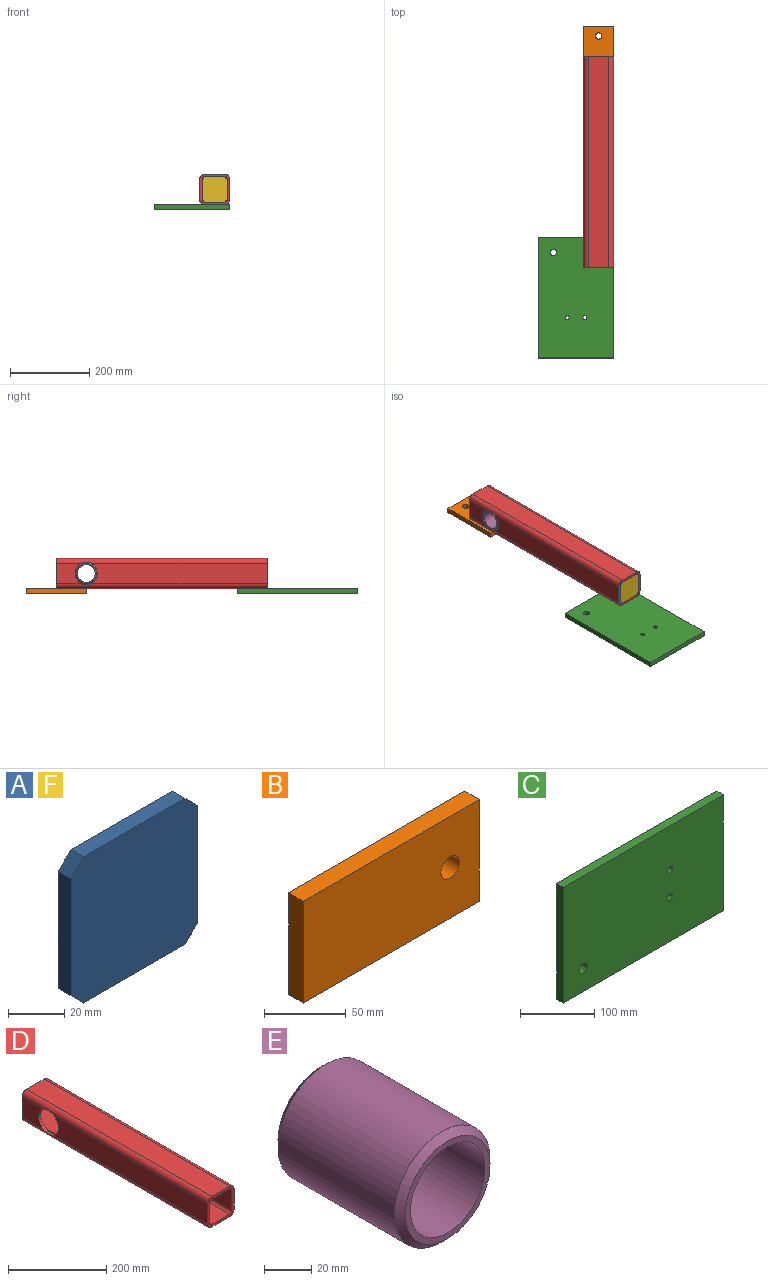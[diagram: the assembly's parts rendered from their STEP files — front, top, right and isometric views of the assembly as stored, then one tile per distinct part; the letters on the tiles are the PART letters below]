
ASSEMBLY  parts=6 mates=5
PART A: 10 faces, bbox 63.5x6.4x63.5 mm
  f0: plane 50.8x6.35mm, normal (1,0,0), area 322.6mm2, adj f4,f5,f6,f9
  f1: plane 50.8x6.35mm, normal (0,0,1), area 322.6mm2, adj f4,f5,f8,f9
  f2: plane 50.8x6.35mm, normal (-1,0,0), area 322.6mm2, adj f4,f5,f7,f8
  f3: plane 50.8x6.35mm, normal (0,0,-1), area 322.6mm2, adj f4,f5,f6,f7
  f4: plane 63.5x63.5mm, normal (0,1,0), area 3951.6mm2, adj f0,f1,f2,f3,f6,f7,f8,f9
  f5: plane 63.5x63.5mm, normal (0,-1,0), area 3951.6mm2, adj f0,f1,f2,f3,f6,f7,f8,f9
  f6: plane 6.35x6.35mm, normal (0.71,0,-0.71), area 57mm2, adj f0,f3,f4,f5
  f7: plane 6.35x6.35mm, normal (-0.71,0,-0.71), area 57mm2, adj f2,f3,f4,f5
  f8: plane 6.35x6.35mm, normal (-0.71,0,0.71), area 57mm2, adj f1,f2,f4,f5
  f9: plane 6.35x6.35mm, normal (0.71,0,0.71), area 57mm2, adj f0,f1,f4,f5
PART B: 7 faces, bbox 152.4x12.7x76.2 mm
  f0: plane 152.4x12.7mm, normal (0,0,1), area 1935.5mm2, adj f1,f3,f4,f5
  f1: plane 76.2x12.7mm, normal (-1,0,0), area 967.7mm2, adj f0,f2,f4,f5
  f2: plane 152.4x12.7mm, normal (0,0,-1), area 1935.5mm2, adj f1,f3,f4,f5
  f3: plane 76.2x12.7mm, normal (1,0,0), area 967.7mm2, adj f0,f2,f4,f5
  f4: plane 152.4x76.2mm, normal (0,1,0), area 11414.9mm2, adj f0,f1,f2,f3,f6
  f5: plane 152.4x76.2mm, normal (0,-1,0), area 11414.9mm2, adj f0,f1,f2,f3,f6
  f6: cylinder r=7.94mm len=15.88mm, axis (0,-1,0), area 633.4mm2, adj f4,f5
PART C: 9 faces, bbox 304.8x12.7x190.5 mm
  f0: plane 304.8x12.7mm, normal (0,0,1), area 3871mm2, adj f1,f3,f4,f5
  f1: plane 190.5x12.7mm, normal (-1,0,0), area 2419.3mm2, adj f0,f2,f4,f5
  f2: plane 304.8x12.7mm, normal (0,0,-1), area 3871mm2, adj f1,f3,f4,f5
  f3: plane 190.5x12.7mm, normal (1,0,0), area 2419.3mm2, adj f0,f2,f4,f5
  f4: plane 304.8x190.5mm, normal (0,1,0), area 57699.2mm2, adj f0,f1,f2,f3,f6,f7,f8
  f5: plane 304.8x190.5mm, normal (0,-1,0), area 57699.2mm2, adj f0,f1,f2,f3,f6,f7,f8
  f6: cylinder r=5.16mm len=12.7mm, axis (0,-1,0), area 411.7mm2, adj f4,f5
  f7: cylinder r=5.16mm len=12.7mm, axis (0,-1,0), area 411.7mm2, adj f4,f5
  f8: cylinder r=7.94mm len=15.88mm, axis (0,1,0), area 633.4mm2, adj f4,f5
PART D: 24 faces, bbox 76.2x533.4x76.2 mm
  f0: plane 63.11x50.8mm, normal (1,0,0), area 2644.4mm2, adj f5,f19,f20,f22
  f1: plane 444.11x50.8mm, normal (1,0,0), area 21999.2mm2, adj f5,f19,f21,f22
  f2: plane 63.11x50.8mm, normal (-1,0,0), area 2644.4mm2, adj f7,f9,f20,f23
  f3: plane 63.11x50.8mm, normal (-1,0,0), area 2644.4mm2, adj f13,f15,f20,f22
  f4: plane 63.11x50.8mm, normal (1,0,0), area 2644.4mm2, adj f11,f17,f20,f23
  f5: cylinder r=12.7mm len=533.4mm, axis (0,-1,0), area 10584.4mm2, adj f0,f1,f6,f20,f21,f22
  f6: plane 533.4x50.8mm, normal (0,0,1), area 27096.7mm2, adj f5,f7,f20,f21
  f7: cylinder r=12.7mm len=533.4mm, axis (0,-1,0), area 10584.4mm2, adj f2,f6,f8,f20,f21,f23
  f8: plane 444.11x50.8mm, normal (-1,0,0), area 21999.2mm2, adj f7,f9,f21,f23
  f9: cylinder r=12.7mm len=533.4mm, axis (0,-1,0), area 10584.4mm2, adj f2,f8,f10,f20,f21,f23
  f10: plane 533.4x50.8mm, normal (0,0,-1), area 27096.7mm2, adj f9,f19,f20,f21
  f11: cylinder r=6.35mm len=533.4mm, axis (0,-1,0), area 5262.6mm2, adj f4,f12,f18,f20,f21,f23
  f12: plane 533.4x50.8mm, normal (0,0,-1), area 27096.7mm2, adj f11,f13,f20,f21
  f13: cylinder r=6.35mm len=533.4mm, axis (0,-1,0), area 5262.6mm2, adj f3,f12,f14,f20,f21,f22
  f14: plane 444.11x50.8mm, normal (-1,0,0), area 21999.2mm2, adj f13,f15,f21,f22
  f15: cylinder r=6.35mm len=533.4mm, axis (0,-1,0), area 5262.6mm2, adj f3,f14,f16,f20,f21,f22
  f16: plane 533.4x50.8mm, normal (0,0,1), area 27096.7mm2, adj f15,f17,f20,f21
  f17: cylinder r=6.35mm len=533.4mm, axis (0,-1,0), area 5262.6mm2, adj f4,f16,f18,f20,f21,f23
  f18: plane 444.11x50.8mm, normal (1,0,0), area 21999.2mm2, adj f11,f17,f21,f23
  f19: cylinder r=12.7mm len=533.4mm, axis (0,-1,0), area 10584.4mm2, adj f0,f1,f10,f20,f21,f22
  f20: plane 76.2x76.2mm, normal (0,1,0), area 1670.4mm2, adj f0,f2,f3,f4,f5,f6,f7,f9
  f21: plane 76.2x76.2mm, normal (0,-1,0), area 1670.4mm2, adj f1,f5,f6,f7,f8,f9,f10,f11
  f22: cylinder r=28.57mm len=57.15mm, axis (1,0,0), area 1152.6mm2, adj f0,f1,f3,f5,f13,f14,f15,f19
  f23: cylinder r=28.57mm len=57.15mm, axis (1,0,0), area 1152.6mm2, adj f2,f4,f7,f8,f9,f11,f17,f18
PART E: 6 faces, bbox 57.2x76.2x57.2 mm
  f0: cylinder r=22.23mm len=76.2mm, axis (0,-1,0), area 10640.9mm2, adj f2,f3
  f1: cylinder r=28.57mm len=69.6mm, axis (0,-1,0), area 12495.4mm2, adj f4,f5
  f2: plane 50.55x50.55mm, normal (0,1,0), area 454.8mm2, adj f0,f4
  f3: plane 50.55x50.55mm, normal (0,-1,0), area 454.8mm2, adj f0,f5
  f4: cone r=28.57mm half-angle=45deg, axis (0,-1,0), area 790mm2, adj f1,f2
  f5: cone r=25.27mm half-angle=45deg, axis (0,1,0), area 790mm2, adj f1,f3
PART F: same geometry as A
PLACE A t=(249.02,527.05,122.52)mm
PLACE B rot(axis=(0.58,0.58,0.58),120deg) t=(104.28,868.79,-50.8)mm
PLACE C rot(axis=(-0.58,0.58,-0.58),120deg) t=(-157.21,-419.24,-38.1)mm
PLACE D at identity
PLACE E rot(axis=(-0.58,0.58,0.58),120deg) t=(155.61,572.2,0)mm
PLACE F t=(249.02,0,122.52)mm
MATE fastened E.f0 <-> D.f22  axis (1,0,0) through (155.61,457.2,0)mm
MATE fastened F.f5 <-> D.f21  axis (0,-1,0) through (117.51,0,0)mm
MATE fastened A.f4 <-> D.f20  axis (0,1,0) through (117.51,533.4,0)mm
MATE fastened B.f4 <-> D.f10  axis (0,0,1) through (117.51,457.2,-38.1)mm
MATE fastened C.f5 <-> D.f10  axis (0,0,1) through (155.61,76.2,-38.1)mm
